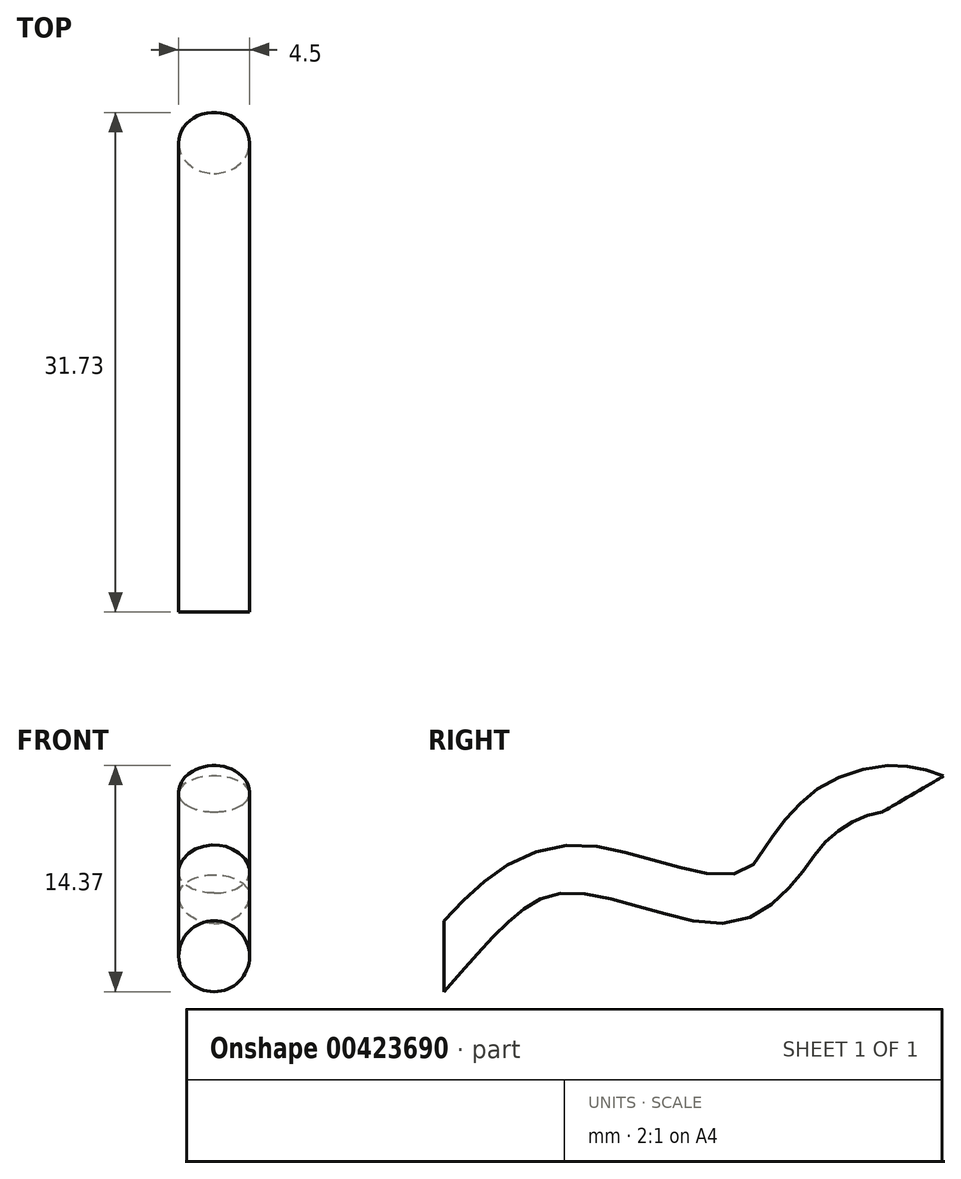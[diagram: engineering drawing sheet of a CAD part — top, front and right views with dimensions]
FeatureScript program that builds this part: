
annotation { "Feature Type Name" : "Feature", "Feature Type Description" : "" }
export const myFeature = defineFeature(function(context is Context, id is Id, definition is map)
    precondition{}
    {
        {
            var Q0;
            Q0=qCreatedBy(makeId("Right.planeOp"),FACE);
            var sketch = newSketch(context, id + "F0", { "sketchPlane" : qUnion([Q0])});
            skFitSpline(sketch, "E0", {"points": [v(0, 17.75) * mm, v(7.87, 23.12) * mm, v(18.32, 21.68) * mm, v(23.84, 26.4) * mm, v(29.8, 28.06) * mm], "startDerivative": vector(25.58, 28.14) * mm, "endDerivative": vector(27.56, -5.82) * mm});
            skSolve(sketch);
        }
        {
            var Q0;
            Q0=qCreatedBy(makeId("Front.planeOp"),FACE);
            var sketch = newSketch(context, id + "F1", { "sketchPlane" : qUnion([Q0])});
            skCircle(sketch, "E1", {"center": v(0, 17.75) * mm, "radius": 2.25 * mm});
            skSolve(sketch);
        }
        {
            var Q0;
            Q0=makeQuery(id+"F1.imprint","IMPRINT",FACE,{"disambiguationData":[TD([[makeQuery(id+"F1.imprint","IMPRINT",EDGE,{"derivedFrom":sQuery(id+"F1.wireOp",EDGE,"E1")}),1.0]])]});
            var Q1;
            Q1=sQuery(id+"F0.wireOp",EDGE,"E0");
            sweep(context, id + "F2", {"profiles" : qUnion([Q0]), "path" : qUnion([Q1])});
        }
    });
